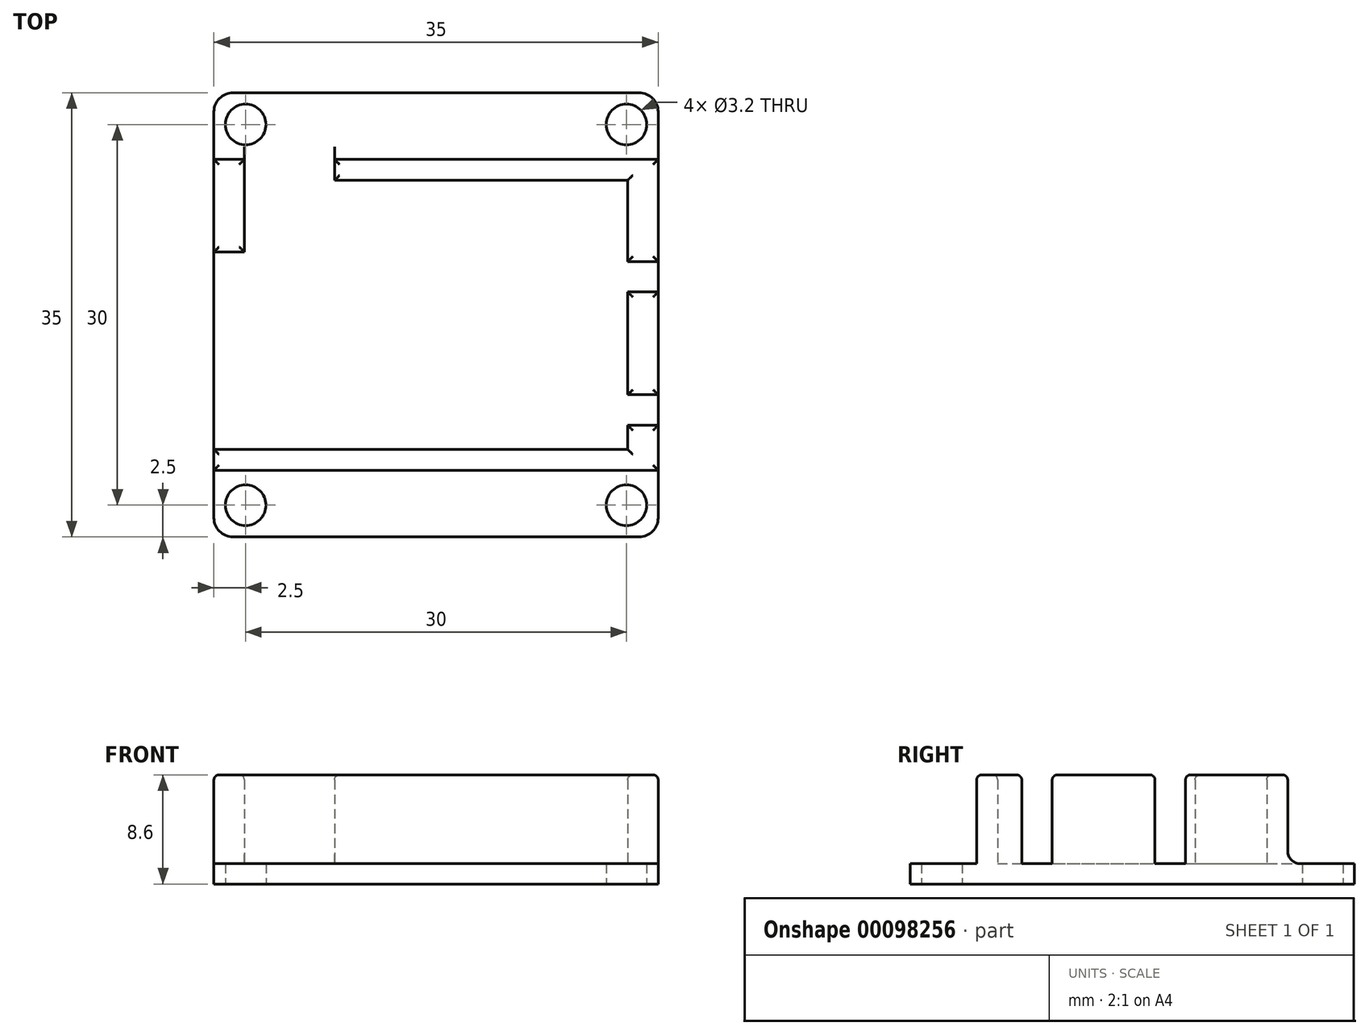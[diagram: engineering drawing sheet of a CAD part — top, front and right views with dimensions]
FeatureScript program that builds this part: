
annotation { "Feature Type Name" : "Feature", "Feature Type Description" : "" }
export const myFeature = defineFeature(function(context is Context, id is Id, definition is map)
    precondition{}
    {
        {
            var Q0;
            Q0=qCreatedBy(makeId("Top.planeOp"),FACE);
            var sketch = newSketch(context, id + "F0", { "sketchPlane" : qUnion([Q0])});
            skLineSegment(sketch, "E0.bottom", {"start": v(-16, -17.5) * mm, "end": v(16, -17.5) * mm});
            skLineSegment(sketch, "E0.top", {"start": v(-16, 17.5) * mm, "end": v(16, 17.5) * mm});
            skLineSegment(sketch, "E0.left", {"start": v(-17.5, -16) * mm, "end": v(-17.5, 16) * mm});
            skLineSegment(sketch, "E0.right", {"start": v(17.5, -16) * mm, "end": v(17.5, 16) * mm});
            skPoint(sketch, "E0.middle", {"position": v(0, 0) * mm});
            skLineSegment(sketch, "E1.bottom", {"start": v(-15, -15) * mm, "end": v(15, -15) * mm, "construction": true});
            skLineSegment(sketch, "E1.top", {"start": v(-15, 15) * mm, "end": v(15, 15) * mm, "construction": true});
            skLineSegment(sketch, "E1.left", {"start": v(-15, -15) * mm, "end": v(-15, 15) * mm, "construction": true});
            skLineSegment(sketch, "E1.right", {"start": v(15, -15) * mm, "end": v(15, 15) * mm, "construction": true});
            skCircle(sketch, "E2", {"center": v(-15, 15) * mm, "radius": 1.6 * mm});
            skCircle(sketch, "E3.MirrorC", {"center": v(15, 15) * mm, "radius": 1.6 * mm});
            skCircle(sketch, "E4", {"center": v(-15, -15) * mm, "radius": 1.6 * mm});
            skCircle(sketch, "E5.MirrorC", {"center": v(15, -15) * mm, "radius": 1.6 * mm});
            skPoint(sketch, "E6.visualSharp", {"position": v(-17.5, 17.5) * mm});
            skArc(sketch, "E6.filletArc", {"start": v(-16, 17.5) * mm, "mid": v(-17.06, 17.06) * mm, "end": v(-17.5, 16) * mm});
            skPoint(sketch, "E7.visualSharp", {"position": v(17.5, 17.5) * mm});
            skArc(sketch, "E7.filletArc", {"start": v(17.5, 16) * mm, "mid": v(17.06, 17.06) * mm, "end": v(16, 17.5) * mm});
            skPoint(sketch, "E8.visualSharp", {"position": v(17.5, -17.5) * mm});
            skArc(sketch, "E8.filletArc", {"start": v(16, -17.5) * mm, "mid": v(17.06, -17.06) * mm, "end": v(17.5, -16) * mm});
            skPoint(sketch, "E9.visualSharp", {"position": v(-17.5, -17.5) * mm});
            skArc(sketch, "E9.filletArc", {"start": v(-17.5, -16) * mm, "mid": v(-17.06, -17.06) * mm, "end": v(-16, -17.5) * mm});
            skSolve(sketch);
        }
        {
            var Q0;
            Q0=makeQuery(id+"F0.imprint","IMPRINT",FACE,{"disambiguationData":[TD([[makeQuery(id+"F0.imprint","IMPRINT",EDGE,{"derivedFrom":sQuery(id+"F0.wireOp",EDGE,"E0.bottom")}),1.0]])]});
            extrude(context, id + "F1", {"entities" : qUnion([Q0]), "depth" : 1.6 * mm});
        }
        {
            var Q0;
            Q0=makeQuery(id+"F1.opExtrude","CAP_FACE",FACE,{"disambiguationData":[OSD([sQuery(id+"F0.wireOp",EDGE,"E0.bottom"),sQuery(id+"F0.wireOp",EDGE,"E0.top"),sQuery(id+"F0.wireOp",EDGE,"E0.left"),sQuery(id+"F0.wireOp",EDGE,"E0.right"),sQuery(id+"F0.wireOp",EDGE,"E2"),sQuery(id+"F0.wireOp",EDGE,"E3.MirrorC"),sQuery(id+"F0.wireOp",EDGE,"E4"),sQuery(id+"F0.wireOp",EDGE,"E5.MirrorC")])],"isStart":false});
            var sketch = newSketch(context, id + "F2", { "sketchPlane" : qUnion([Q0])});
            skLineSegment(sketch, "E10.bottom", {"start": v(-15.1, -10.6) * mm, "end": v(15.1, -10.6) * mm});
            skLineSegment(sketch, "E10.top", {"start": v(-15.1, 10.6) * mm, "end": v(15.1, 10.6) * mm});
            skLineSegment(sketch, "E10.left", {"start": v(-15.1, -10.6) * mm, "end": v(-15.1, 10.6) * mm});
            skLineSegment(sketch, "E10.right", {"start": v(15.1, -10.6) * mm, "end": v(15.1, 10.6) * mm});
            skPoint(sketch, "E10.middle", {"position": v(0, 0) * mm});
            skLineSegment(sketch, "E11.bottom", {"start": v(-17.5, -12.25) * mm, "end": v(17.5, -12.25) * mm});
            skLineSegment(sketch, "E11.top", {"start": v(-17.5, 12.25) * mm, "end": v(17.5, 12.25) * mm});
            skLineSegment(sketch, "E11.left", {"start": v(-17.5, -12.25) * mm, "end": v(-17.5, 12.25) * mm});
            skLineSegment(sketch, "E11.right", {"start": v(17.5, -12.25) * mm, "end": v(17.5, 12.25) * mm});
            skLineSegment(sketch, "E12", {"start": v(15.1, 4.2) * mm, "end": v(17.5, 4.2) * mm});
            skLineSegment(sketch, "E13", {"start": v(15.1, 1.8) * mm, "end": v(17.5, 1.8) * mm});
            skLineSegment(sketch, "E14", {"start": v(15.1, -6.3) * mm, "end": v(17.5, -6.3) * mm});
            skLineSegment(sketch, "E15", {"start": v(15.1, -8.7) * mm, "end": v(17.5, -8.7) * mm});
            skLineSegment(sketch, "E16", {"start": v(-15.1, 10.6) * mm, "end": v(-15.1, 12.25) * mm});
            skLineSegment(sketch, "E17", {"start": v(-8, 10.6) * mm, "end": v(-8, 12.25) * mm});
            skLineSegment(sketch, "E18", {"start": v(-15.1, -10.6) * mm, "end": v(-15.1, -12.25) * mm});
            skLineSegment(sketch, "E19", {"start": v(-15.1, 4.95) * mm, "end": v(-17.5, 4.95) * mm});
            skLineSegment(sketch, "E20", {"start": v(-15.1, -10.6) * mm, "end": v(-17.5, -10.6) * mm});
            skSolve(sketch);
        }
        {
            var Q0;
            {var subQ5=sQuery(id+"F2.wireOp",EDGE,"E10.bottom");Q0=makeQuery(id+"F2.imprint","IMPRINT",FACE,{"disambiguationData":[TD([[makeQuery(id+"F2.imprint","IMPRINT",EDGE,{"derivedFrom":subQ5}),-1.0]])]});}
            var Q1;
            {var subQ0=sQuery(id+"F2.wireOp",EDGE,"E13");Q1=makeQuery(id+"F2.imprint","IMPRINT",FACE,{"disambiguationData":[TD([[makeQuery(id+"F2.imprint","IMPRINT",EDGE,{"derivedFrom":subQ0}),-1.0]])]});}
            var Q2;
            {var subQ3=sQuery(id+"F2.wireOp",EDGE,"E12");Q2=makeQuery(id+"F2.imprint","IMPRINT",FACE,{"disambiguationData":[TD([[makeQuery(id+"F2.imprint","IMPRINT",EDGE,{"derivedFrom":subQ3}),1.0]])]});}
            var Q3;
            {var subQ0=sQuery(id+"F2.wireOp",EDGE,"E16");Q3=makeQuery(id+"F2.imprint","IMPRINT",FACE,{"disambiguationData":[TD([[makeQuery(id+"F2.imprint","IMPRINT",EDGE,{"derivedFrom":subQ0}),1.0]])]});}
            var Q4;
            {var subQ3=sQuery(id+"F2.wireOp",EDGE,"E18");Q4=makeQuery(id+"F2.imprint","IMPRINT",FACE,{"disambiguationData":[TD([[makeQuery(id+"F2.imprint","IMPRINT",EDGE,{"derivedFrom":subQ3}),-1.0]])]});}
            extrude(context, id + "F3", {"entities" : qUnion([Q0, Q1, Q2, Q3, Q4]), "operationType" : NewBodyOperationType.ADD, "depth" : 7 * mm});
        }
        {
            var Q0;
            Q0=makeQuery(id+"F3.opExtrude","CAP_EDGE",EDGE,{"disambiguationData":[OSD([sQuery(id+"F2.wireOp",EDGE,"E11.bottom")])],"isStart":true});
            var Q1;
            Q1=makeQuery(id+"F3.opExtrude","CAP_EDGE",EDGE,{"disambiguationData":[OSD([sQuery(id+"F2.wireOp",EDGE,"E11.top")])],"isStart":true});
            fillet(context, id + "F4", {"entities" : qUnion([Q0, Q1]), "radius" : 1 * mm, "tangentPropagation" : true, "allowEdgeOverflow" : false});
        }
        {
            var Q0;
            {var subQ0=sQuery(id+"F2.wireOp",EDGE,"E11.top");Q0=makeQuery(id+"F3.opExtrude","CAP_EDGE",EDGE,{"disambiguationData":[OSD([subQ0]),TDD([makeQuery(id+"F2.imprint","IMPRINT",EDGE,{"disambiguationData":[TD([[makeQuery(id+"F2.imprint","INTERSECT",VERTEX,{"derivedFrom":[subQ0,sQuery(id+"F2.wireOp",EDGE,"E17")]}),-1.0]])],"derivedFrom":subQ0})])],"isStart":false});}
            var Q1;
            Q1=makeQuery(id+"F3.opExtrude","CAP_EDGE",EDGE,{"disambiguationData":[OSD([sQuery(id+"F2.wireOp",EDGE,"E10.top")])],"isStart":false});
            var Q2;
            Q2=makeQuery(id+"F3.opExtrude","CAP_EDGE",EDGE,{"disambiguationData":[OSD([sQuery(id+"F2.wireOp",EDGE,"E10.left"),sQuery(id+"F2.wireOp",EDGE,"E16")])],"isStart":false});
            var Q3;
            {var subQ0=sQuery(id+"F2.wireOp",EDGE,"E11.left");Q3=makeQuery(id+"F3.opExtrude","CAP_EDGE",EDGE,{"disambiguationData":[OSD([subQ0]),TDD([makeQuery(id+"F2.imprint","IMPRINT",EDGE,{"disambiguationData":[TD([[makeQuery(id+"F2.imprint","INTERSECT",VERTEX,{"derivedFrom":[subQ0,sQuery(id+"F2.wireOp",EDGE,"E19")]}),-1.0]])],"derivedFrom":subQ0})])],"isStart":false});}
            var Q4;
            {var subQ0=sQuery(id+"F2.wireOp",EDGE,"E11.top");Q4=makeQuery(id+"F3.opExtrude","CAP_EDGE",EDGE,{"disambiguationData":[OSD([subQ0]),TDD([makeQuery(id+"F2.imprint","IMPRINT",EDGE,{"disambiguationData":[TD([[makeQuery(id+"F2.imprint","INTERSECT",VERTEX,{"derivedFrom":[subQ0,sQuery(id+"F2.wireOp",EDGE,"E16")]}),1.0]])],"derivedFrom":subQ0})])],"isStart":false});}
            var Q5;
            Q5=makeQuery(id+"F3.opExtrude","CAP_EDGE",EDGE,{"disambiguationData":[OSD([sQuery(id+"F2.wireOp",EDGE,"E17")])],"isStart":false});
            var Q6;
            Q6=makeQuery(id+"F3.opExtrude","CAP_EDGE",EDGE,{"disambiguationData":[OSD([sQuery(id+"F2.wireOp",EDGE,"E19")])],"isStart":false});
            var Q7;
            Q7=makeQuery(id+"F3.opExtrude","CAP_EDGE",EDGE,{"disambiguationData":[OSD([sQuery(id+"F2.wireOp",EDGE,"E10.bottom"),sQuery(id+"F2.wireOp",EDGE,"E20")])],"isStart":false});
            var Q8;
            Q8=makeQuery(id+"F3.opExtrude","CAP_EDGE",EDGE,{"disambiguationData":[OSD([sQuery(id+"F2.wireOp",EDGE,"E11.bottom")])],"isStart":false});
            var Q9;
            Q9=makeQuery(id+"F3.opExtrude","CAP_EDGE",EDGE,{"disambiguationData":[OSD([sQuery(id+"F2.wireOp",EDGE,"E15")])],"isStart":false});
            var Q10;
            {var subQ0=sQuery(id+"F2.wireOp",EDGE,"E11.right");Q10=makeQuery(id+"F3.opExtrude","CAP_EDGE",EDGE,{"disambiguationData":[OSD([subQ0]),TDD([makeQuery(id+"F2.imprint","IMPRINT",EDGE,{"disambiguationData":[TD([[makeQuery(id+"F2.imprint","INTERSECT",VERTEX,{"derivedFrom":[subQ0,sQuery(id+"F2.wireOp",EDGE,"E15")]}),1.0]])],"derivedFrom":subQ0})])],"isStart":false});}
            var Q11;
            {var subQ0=sQuery(id+"F2.wireOp",EDGE,"E10.right");Q11=makeQuery(id+"F3.opExtrude","CAP_EDGE",EDGE,{"disambiguationData":[OSD([subQ0]),TDD([makeQuery(id+"F2.imprint","IMPRINT",EDGE,{"disambiguationData":[TD([[makeQuery(id+"F2.imprint","INTERSECT",VERTEX,{"derivedFrom":[sQuery(id+"F2.wireOp",EDGE,"E10.bottom"),subQ0]}),-1.0]])],"derivedFrom":subQ0})])],"isStart":false});}
            var Q12;
            Q12=makeQuery(id+"F3.opExtrude","CAP_EDGE",EDGE,{"disambiguationData":[OSD([sQuery(id+"F2.wireOp",EDGE,"E14")])],"isStart":false});
            var Q13;
            {var subQ0=sQuery(id+"F2.wireOp",EDGE,"E10.right");Q13=makeQuery(id+"F3.opExtrude","CAP_EDGE",EDGE,{"disambiguationData":[OSD([subQ0]),TDD([makeQuery(id+"F2.imprint","IMPRINT",EDGE,{"disambiguationData":[TD([[makeQuery(id+"F2.imprint","INTERSECT",VERTEX,{"derivedFrom":[subQ0,sQuery(id+"F2.wireOp",EDGE,"E13")]}),1.0]])],"derivedFrom":subQ0})])],"isStart":false});}
            var Q14;
            {var subQ0=sQuery(id+"F2.wireOp",EDGE,"E11.right");Q14=makeQuery(id+"F3.opExtrude","CAP_EDGE",EDGE,{"disambiguationData":[OSD([subQ0]),TDD([makeQuery(id+"F2.imprint","IMPRINT",EDGE,{"disambiguationData":[TD([[makeQuery(id+"F2.imprint","INTERSECT",VERTEX,{"derivedFrom":[subQ0,sQuery(id+"F2.wireOp",EDGE,"E13")]}),1.0]])],"derivedFrom":subQ0})])],"isStart":false});}
            var Q15;
            Q15=makeQuery(id+"F3.opExtrude","CAP_EDGE",EDGE,{"disambiguationData":[OSD([sQuery(id+"F2.wireOp",EDGE,"E13")])],"isStart":false});
            var Q16;
            Q16=makeQuery(id+"F3.opExtrude","CAP_EDGE",EDGE,{"disambiguationData":[OSD([sQuery(id+"F2.wireOp",EDGE,"E12")])],"isStart":false});
            var Q17;
            {var subQ0=sQuery(id+"F2.wireOp",EDGE,"E10.right");Q17=makeQuery(id+"F3.opExtrude","CAP_EDGE",EDGE,{"disambiguationData":[OSD([subQ0]),TDD([makeQuery(id+"F2.imprint","IMPRINT",EDGE,{"disambiguationData":[TD([[makeQuery(id+"F2.imprint","INTERSECT",VERTEX,{"derivedFrom":[sQuery(id+"F2.wireOp",EDGE,"E10.top"),subQ0]}),1.0]])],"derivedFrom":subQ0})])],"isStart":false});}
            var Q18;
            {var subQ0=sQuery(id+"F2.wireOp",EDGE,"E11.right");Q18=makeQuery(id+"F3.opExtrude","CAP_EDGE",EDGE,{"disambiguationData":[OSD([subQ0]),TDD([makeQuery(id+"F2.imprint","IMPRINT",EDGE,{"disambiguationData":[TD([[makeQuery(id+"F2.imprint","INTERSECT",VERTEX,{"derivedFrom":[subQ0,sQuery(id+"F2.wireOp",EDGE,"E12")]}),-1.0]])],"derivedFrom":subQ0})])],"isStart":false});}
            var Q19;
            {var subQ0=sQuery(id+"F2.wireOp",EDGE,"E11.left");Q19=makeQuery(id+"F3.opExtrude","CAP_EDGE",EDGE,{"disambiguationData":[OSD([subQ0]),TDD([makeQuery(id+"F2.imprint","IMPRINT",EDGE,{"disambiguationData":[TD([[makeQuery(id+"F2.imprint","INTERSECT",VERTEX,{"derivedFrom":[subQ0,sQuery(id+"F2.wireOp",EDGE,"E20")]}),1.0]])],"derivedFrom":subQ0})])],"isStart":false});}
            fillet(context, id + "F5", {"entities" : qUnion([Q0, Q1, Q2, Q3, Q4, Q5, Q6, Q7, Q8, Q9, Q10, Q11, Q12, Q13, Q14, Q15, Q16, Q17, Q18, Q19]), "radius" : .4 * mm, "tangentPropagation" : true, "allowEdgeOverflow" : false});
        }
    });
